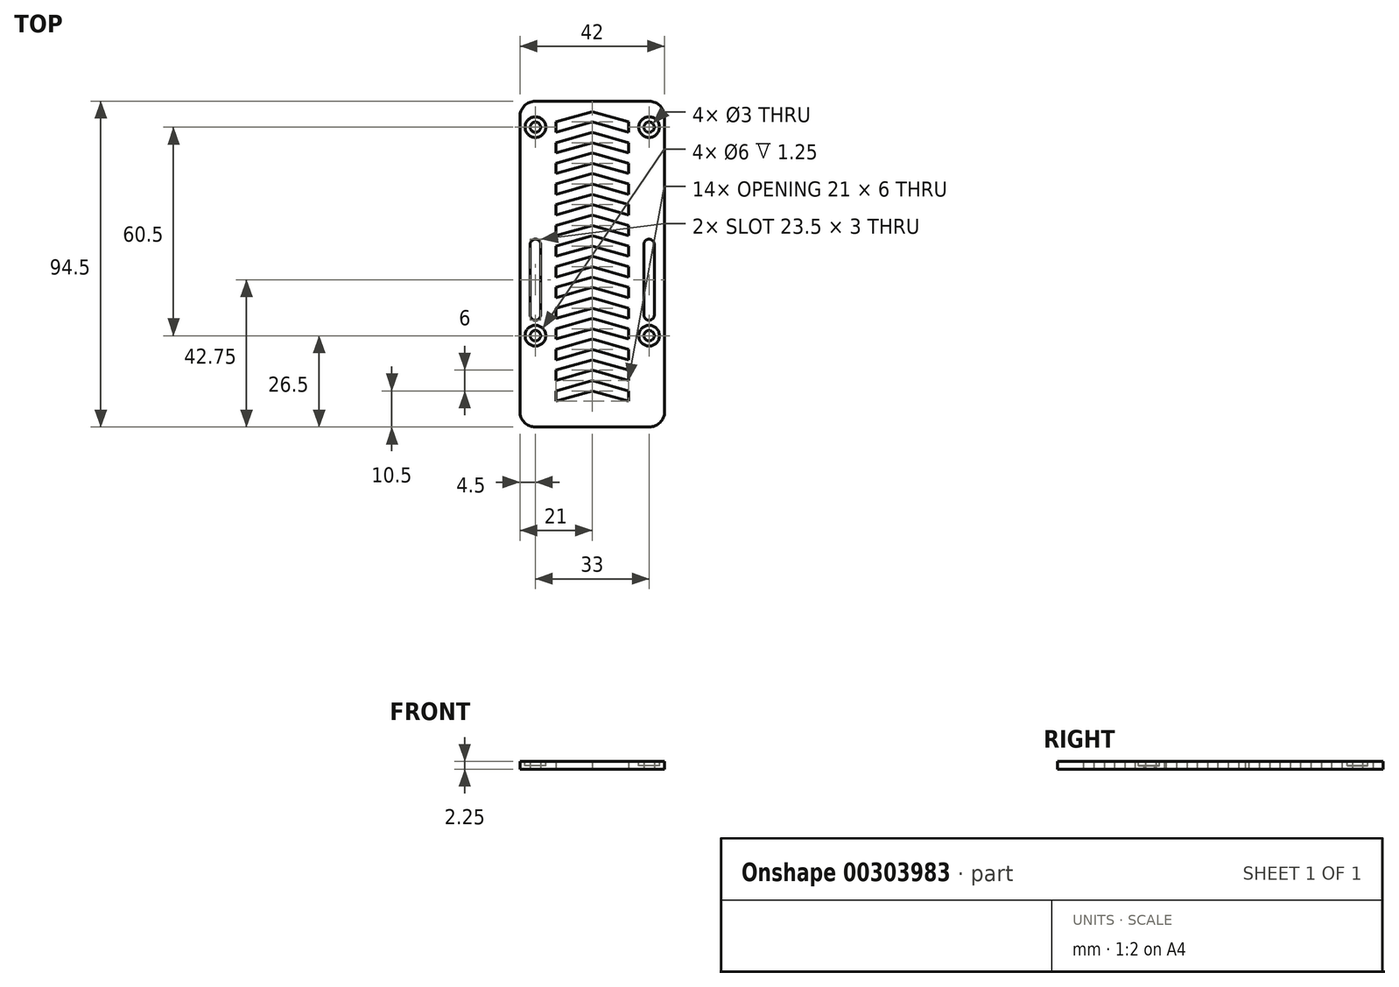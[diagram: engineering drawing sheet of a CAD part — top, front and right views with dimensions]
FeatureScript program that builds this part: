
annotation { "Feature Type Name" : "Feature", "Feature Type Description" : "" }
export const myFeature = defineFeature(function(context is Context, id is Id, definition is map)
    precondition{}
    {
        {
            var Q0;
            Q0=qCreatedBy(makeId("Top.planeOp"),FACE);
            var sketch = newSketch(context, id + "F0", { "sketchPlane" : qUnion([Q0])});
            skLineSegment(sketch, "E0.left", {"start": v(-21, 35.25) * mm, "end": v(-21, -44.25) * mm});
            skLineSegment(sketch, "E0.right", {"start": v(21, 35.25) * mm, "end": v(21, -44.25) * mm});
            skLineSegment(sketch, "E1", {"start": v(-16.5, -0.25) * mm, "end": v(-16.5, -0.25) * mm});
            skLineSegment(sketch, "E2", {"start": v(-16.5, -23.75) * mm, "end": v(-16.5, -23.75) * mm});
            skLineSegment(sketch, "E3", {"start": v(16.5, -23.75) * mm, "end": v(16.5, -23.75) * mm});
            skLineSegment(sketch, "E4", {"start": v(16.5, -0.25) * mm, "end": v(16.5, -0.25) * mm});
            skLineSegment(sketch, "E5.trimOffspring", {"start": v(18, -1.75) * mm, "end": v(18, -22.25) * mm});
            skLineSegment(sketch, "E6.trimOffspring", {"start": v(15, -1.75) * mm, "end": v(15, -22.25) * mm});
            skLineSegment(sketch, "E7.trimOffspring", {"start": v(-15, -1.75) * mm, "end": v(-15, -22.25) * mm});
            skLineSegment(sketch, "E8.trimOffspring", {"start": v(-18, -1.75) * mm, "end": v(-18, -22.25) * mm});
            skCircle(sketch, "E9", {"center": v(16.5, 32.25) * mm, "radius": 1.5 * mm});
            skCircle(sketch, "E10", {"center": v(-16.5, 32.25) * mm, "radius": 1.5 * mm});
            skPoint(sketch, "E11.visualSharp", {"position": v(18, -0.25) * mm});
            skArc(sketch, "E11.filletArc", {"start": v(18, -1.75) * mm, "mid": v(17.56, -0.69) * mm, "end": v(16.5, -0.25) * mm});
            skPoint(sketch, "E12.visualSharp", {"position": v(15, -0.25) * mm});
            skArc(sketch, "E12.filletArc", {"start": v(16.5, -0.25) * mm, "mid": v(15.44, -0.69) * mm, "end": v(15, -1.75) * mm});
            skPoint(sketch, "E13.visualSharp", {"position": v(-15, -0.25) * mm});
            skArc(sketch, "E13.filletArc", {"start": v(-15, -1.75) * mm, "mid": v(-15.44, -0.69) * mm, "end": v(-16.5, -0.25) * mm});
            skPoint(sketch, "E14.visualSharp", {"position": v(-18, -0.25) * mm});
            skArc(sketch, "E14.filletArc", {"start": v(-16.5, -0.25) * mm, "mid": v(-17.56, -0.69) * mm, "end": v(-18, -1.75) * mm});
            skCircle(sketch, "E15", {"center": v(16.5, -28.25) * mm, "radius": 1.5 * mm});
            skPoint(sketch, "E15.centerSnap0", {"position": v(16.5, -23.75) * mm});
            skCircle(sketch, "E16", {"center": v(-16.5, -28.25) * mm, "radius": 1.5 * mm});
            skPoint(sketch, "E16.centerSnap0", {"position": v(-16.5, -23.75) * mm});
            skPoint(sketch, "E17.visualSharp", {"position": v(18, -23.75) * mm});
            skArc(sketch, "E17.filletArc", {"start": v(16.5, -23.75) * mm, "mid": v(17.56, -23.31) * mm, "end": v(18, -22.25) * mm});
            skPoint(sketch, "E18.visualSharp", {"position": v(-15, -23.75) * mm});
            skArc(sketch, "E18.filletArc", {"start": v(-16.5, -23.75) * mm, "mid": v(-15.44, -23.31) * mm, "end": v(-15, -22.25) * mm});
            skPoint(sketch, "E19.visualSharp", {"position": v(-18, -23.75) * mm});
            skArc(sketch, "E19.filletArc", {"start": v(-18, -22.25) * mm, "mid": v(-17.56, -23.31) * mm, "end": v(-16.5, -23.75) * mm});
            skPoint(sketch, "E20.visualSharp", {"position": v(15, -23.75) * mm});
            skArc(sketch, "E20.filletArc", {"start": v(15, -22.25) * mm, "mid": v(15.44, -23.31) * mm, "end": v(16.5, -23.75) * mm});
            skPoint(sketch, "E21", {"position": v(-21, -54.75) * mm});
            skLineSegment(sketch, "E22", {"start": v(-21, -44.25) * mm, "end": v(-21, -50.25) * mm});
            skLineSegment(sketch, "E23", {"start": v(21, -44.25) * mm, "end": v(21, -50.25) * mm});
            skLineSegment(sketch, "E24", {"start": v(16.5, -54.75) * mm, "end": v(-16.5, -54.75) * mm});
            skArc(sketch, "E25.filletArc", {"start": v(-21, -50.25) * mm, "mid": v(-19.68, -53.43) * mm, "end": v(-16.5, -54.75) * mm});
            skPoint(sketch, "E26.visualSharp", {"position": v(21, -54.75) * mm});
            skArc(sketch, "E26.filletArc", {"start": v(16.5, -54.75) * mm, "mid": v(19.68, -53.43) * mm, "end": v(21, -50.25) * mm});
            skLineSegment(sketch, "E27", {"start": v(-16.5, 39.75) * mm, "end": v(16.5, 39.75) * mm});
            skPoint(sketch, "E28.visualSharp", {"position": v(-21, 39.75) * mm});
            skArc(sketch, "E28.filletArc", {"start": v(-16.5, 39.75) * mm, "mid": v(-19.68, 38.43) * mm, "end": v(-21, 35.25) * mm});
            skPoint(sketch, "E29.visualSharp", {"position": v(21, 39.75) * mm});
            skArc(sketch, "E29.filletArc", {"start": v(21, 35.25) * mm, "mid": v(19.68, 38.43) * mm, "end": v(16.5, 39.75) * mm});
            skCircle(sketch, "E30", {"center": v(-16.5, 32.25) * mm, "radius": 3 * mm, "construction": true});
            skCircle(sketch, "E31", {"center": v(16.5, 32.25) * mm, "radius": 3 * mm, "construction": true});
            skPoint(sketch, "E32", {"position": v(-10.5, 36.75) * mm});
            skPoint(sketch, "E33", {"position": v(-10.5, 33.75) * mm});
            skPoint(sketch, "E34", {"position": v(-10.5, 30.75) * mm});
            skPoint(sketch, "E35", {"position": v(-10.5, 27.75) * mm});
            skPoint(sketch, "E36", {"position": v(-10.5, 24.75) * mm});
            skLineSegment(sketch, "E37", {"start": v(0, 36.75) * mm, "end": v(-10.5, 33.75) * mm});
            skPoint(sketch, "E37.startSnap0", {"position": v(0, 39.75) * mm});
            skLineSegment(sketch, "E38", {"start": v(-10.5, 30.75) * mm, "end": v(-10.5, 33.75) * mm});
            skLineSegment(sketch, "E39", {"start": v(0, 33.75) * mm, "end": v(-10.5, 30.75) * mm});
            skLineSegment(sketch, "E40", {"start": v(0, 33.75) * mm, "end": v(10.5, 30.75) * mm});
            skLineSegment(sketch, "E41", {"start": v(10.5, 30.75) * mm, "end": v(10.5, 33.75) * mm});
            skLineSegment(sketch, "E42", {"start": v(10.5, 33.75) * mm, "end": v(0, 36.75) * mm});
            skLineSegment(sketch, "E43.1.0.0", {"start": v(0, 30.75) * mm, "end": v(-10.5, 27.75) * mm});
            skLineSegment(sketch, "E43.1.0.1", {"start": v(-10.5, 24.75) * mm, "end": v(-10.5, 27.75) * mm});
            skLineSegment(sketch, "E43.1.0.2", {"start": v(0, 27.75) * mm, "end": v(-10.5, 24.75) * mm});
            skLineSegment(sketch, "E43.1.0.3", {"start": v(0, 27.75) * mm, "end": v(10.5, 24.75) * mm});
            skLineSegment(sketch, "E43.1.0.4", {"start": v(10.5, 24.75) * mm, "end": v(10.5, 27.75) * mm});
            skLineSegment(sketch, "E43.1.0.5", {"start": v(10.5, 27.75) * mm, "end": v(0, 30.75) * mm});
            skLineSegment(sketch, "E43.2.0.0", {"start": v(0, 24.75) * mm, "end": v(-10.5, 21.75) * mm});
            skLineSegment(sketch, "E43.2.0.1", {"start": v(-10.5, 18.75) * mm, "end": v(-10.5, 21.75) * mm});
            skLineSegment(sketch, "E43.2.0.2", {"start": v(0, 21.75) * mm, "end": v(-10.5, 18.75) * mm});
            skLineSegment(sketch, "E43.2.0.3", {"start": v(0, 21.75) * mm, "end": v(10.5, 18.75) * mm});
            skLineSegment(sketch, "E43.2.0.4", {"start": v(10.5, 18.75) * mm, "end": v(10.5, 21.75) * mm});
            skLineSegment(sketch, "E43.2.0.5", {"start": v(10.5, 21.75) * mm, "end": v(0, 24.75) * mm});
            skLineSegment(sketch, "E43.3.0.0", {"start": v(0, 18.75) * mm, "end": v(-10.5, 15.75) * mm});
            skLineSegment(sketch, "E43.3.0.1", {"start": v(-10.5, 12.75) * mm, "end": v(-10.5, 15.75) * mm});
            skLineSegment(sketch, "E43.3.0.2", {"start": v(0, 15.75) * mm, "end": v(-10.5, 12.75) * mm});
            skLineSegment(sketch, "E43.3.0.3", {"start": v(0, 15.75) * mm, "end": v(10.5, 12.75) * mm});
            skLineSegment(sketch, "E43.3.0.4", {"start": v(10.5, 12.75) * mm, "end": v(10.5, 15.75) * mm});
            skLineSegment(sketch, "E43.3.0.5", {"start": v(10.5, 15.75) * mm, "end": v(0, 18.75) * mm});
            skLineSegment(sketch, "E43.4.0.0", {"start": v(0, 12.75) * mm, "end": v(-10.5, 9.75) * mm});
            skLineSegment(sketch, "E43.4.0.1", {"start": v(-10.5, 6.75) * mm, "end": v(-10.5, 9.75) * mm});
            skLineSegment(sketch, "E43.4.0.2", {"start": v(0, 9.75) * mm, "end": v(-10.5, 6.75) * mm});
            skLineSegment(sketch, "E43.4.0.3", {"start": v(0, 9.75) * mm, "end": v(10.5, 6.75) * mm});
            skLineSegment(sketch, "E43.4.0.4", {"start": v(10.5, 6.75) * mm, "end": v(10.5, 9.75) * mm});
            skLineSegment(sketch, "E43.4.0.5", {"start": v(10.5, 9.75) * mm, "end": v(0, 12.75) * mm});
            skLineSegment(sketch, "E43.5.0.0", {"start": v(0, 6.75) * mm, "end": v(-10.5, 3.75) * mm});
            skLineSegment(sketch, "E43.5.0.1", {"start": v(-10.5, 0.75) * mm, "end": v(-10.5, 3.75) * mm});
            skLineSegment(sketch, "E43.5.0.2", {"start": v(0, 3.75) * mm, "end": v(-10.5, 0.75) * mm});
            skLineSegment(sketch, "E43.5.0.3", {"start": v(0, 3.75) * mm, "end": v(10.5, 0.75) * mm});
            skLineSegment(sketch, "E43.5.0.4", {"start": v(10.5, 0.75) * mm, "end": v(10.5, 3.75) * mm});
            skLineSegment(sketch, "E43.5.0.5", {"start": v(10.5, 3.75) * mm, "end": v(0, 6.75) * mm});
            skLineSegment(sketch, "E43.6.0.0", {"start": v(0, 0.75) * mm, "end": v(-10.5, -2.25) * mm});
            skLineSegment(sketch, "E43.6.0.1", {"start": v(-10.5, -5.25) * mm, "end": v(-10.5, -2.25) * mm});
            skLineSegment(sketch, "E43.6.0.2", {"start": v(0, -2.25) * mm, "end": v(-10.5, -5.25) * mm});
            skLineSegment(sketch, "E43.6.0.3", {"start": v(0, -2.25) * mm, "end": v(10.5, -5.25) * mm});
            skLineSegment(sketch, "E43.6.0.4", {"start": v(10.5, -5.25) * mm, "end": v(10.5, -2.25) * mm});
            skLineSegment(sketch, "E43.6.0.5", {"start": v(10.5, -2.25) * mm, "end": v(0, 0.75) * mm});
            skLineSegment(sketch, "E43.7.0.0", {"start": v(0, -5.25) * mm, "end": v(-10.5, -8.25) * mm});
            skLineSegment(sketch, "E43.7.0.1", {"start": v(-10.5, -11.25) * mm, "end": v(-10.5, -8.25) * mm});
            skLineSegment(sketch, "E43.7.0.2", {"start": v(0, -8.25) * mm, "end": v(-10.5, -11.25) * mm});
            skLineSegment(sketch, "E43.7.0.3", {"start": v(0, -8.25) * mm, "end": v(10.5, -11.25) * mm});
            skLineSegment(sketch, "E43.7.0.4", {"start": v(10.5, -11.25) * mm, "end": v(10.5, -8.25) * mm});
            skLineSegment(sketch, "E43.7.0.5", {"start": v(10.5, -8.25) * mm, "end": v(0, -5.25) * mm});
            skLineSegment(sketch, "E43.8.0.0", {"start": v(0, -11.25) * mm, "end": v(-10.5, -14.25) * mm});
            skLineSegment(sketch, "E43.8.0.1", {"start": v(-10.5, -17.25) * mm, "end": v(-10.5, -14.25) * mm});
            skLineSegment(sketch, "E43.8.0.2", {"start": v(0, -14.25) * mm, "end": v(-10.5, -17.25) * mm});
            skLineSegment(sketch, "E43.8.0.3", {"start": v(0, -14.25) * mm, "end": v(10.5, -17.25) * mm});
            skLineSegment(sketch, "E43.8.0.4", {"start": v(10.5, -17.25) * mm, "end": v(10.5, -14.25) * mm});
            skLineSegment(sketch, "E43.8.0.5", {"start": v(10.5, -14.25) * mm, "end": v(0, -11.25) * mm});
            skLineSegment(sketch, "E43.9.0.0", {"start": v(0, -17.25) * mm, "end": v(-10.5, -20.25) * mm});
            skLineSegment(sketch, "E43.9.0.1", {"start": v(-10.5, -23.25) * mm, "end": v(-10.5, -20.25) * mm});
            skLineSegment(sketch, "E43.9.0.2", {"start": v(0, -20.25) * mm, "end": v(-10.5, -23.25) * mm});
            skLineSegment(sketch, "E43.9.0.3", {"start": v(0, -20.25) * mm, "end": v(10.5, -23.25) * mm});
            skLineSegment(sketch, "E43.9.0.4", {"start": v(10.5, -23.25) * mm, "end": v(10.5, -20.25) * mm});
            skLineSegment(sketch, "E43.9.0.5", {"start": v(10.5, -20.25) * mm, "end": v(0, -17.25) * mm});
            skLineSegment(sketch, "E43.10.0.0", {"start": v(0, -23.25) * mm, "end": v(-10.5, -26.25) * mm});
            skLineSegment(sketch, "E43.10.0.1", {"start": v(-10.5, -29.25) * mm, "end": v(-10.5, -26.25) * mm});
            skLineSegment(sketch, "E43.10.0.2", {"start": v(0, -26.25) * mm, "end": v(-10.5, -29.25) * mm});
            skLineSegment(sketch, "E43.10.0.3", {"start": v(0, -26.25) * mm, "end": v(10.5, -29.25) * mm});
            skLineSegment(sketch, "E43.10.0.4", {"start": v(10.5, -29.25) * mm, "end": v(10.5, -26.25) * mm});
            skLineSegment(sketch, "E43.10.0.5", {"start": v(10.5, -26.25) * mm, "end": v(0, -23.25) * mm});
            skLineSegment(sketch, "E43.11.0.0", {"start": v(0, -29.25) * mm, "end": v(-10.5, -32.25) * mm});
            skLineSegment(sketch, "E43.11.0.1", {"start": v(-10.5, -35.25) * mm, "end": v(-10.5, -32.25) * mm});
            skLineSegment(sketch, "E43.11.0.2", {"start": v(0, -32.25) * mm, "end": v(-10.5, -35.25) * mm});
            skLineSegment(sketch, "E43.11.0.3", {"start": v(0, -32.25) * mm, "end": v(10.5, -35.25) * mm});
            skLineSegment(sketch, "E43.11.0.4", {"start": v(10.5, -35.25) * mm, "end": v(10.5, -32.25) * mm});
            skLineSegment(sketch, "E43.11.0.5", {"start": v(10.5, -32.25) * mm, "end": v(0, -29.25) * mm});
            skLineSegment(sketch, "E43.12.0.0", {"start": v(0, -35.25) * mm, "end": v(-10.5, -38.25) * mm});
            skLineSegment(sketch, "E43.12.0.1", {"start": v(-10.5, -41.25) * mm, "end": v(-10.5, -38.25) * mm});
            skLineSegment(sketch, "E43.12.0.2", {"start": v(0, -38.25) * mm, "end": v(-10.5, -41.25) * mm});
            skLineSegment(sketch, "E43.12.0.3", {"start": v(0, -38.25) * mm, "end": v(10.5, -41.25) * mm});
            skLineSegment(sketch, "E43.12.0.4", {"start": v(10.5, -41.25) * mm, "end": v(10.5, -38.25) * mm});
            skLineSegment(sketch, "E43.12.0.5", {"start": v(10.5, -38.25) * mm, "end": v(0, -35.25) * mm});
            skLineSegment(sketch, "E43.13.0.0", {"start": v(0, -41.25) * mm, "end": v(-10.5, -44.25) * mm});
            skLineSegment(sketch, "E43.13.0.1", {"start": v(-10.5, -47.25) * mm, "end": v(-10.5, -44.25) * mm});
            skLineSegment(sketch, "E43.13.0.2", {"start": v(0, -44.25) * mm, "end": v(-10.5, -47.25) * mm});
            skLineSegment(sketch, "E43.13.0.3", {"start": v(0, -44.25) * mm, "end": v(10.5, -47.25) * mm});
            skLineSegment(sketch, "E43.13.0.4", {"start": v(10.5, -47.25) * mm, "end": v(10.5, -44.25) * mm});
            skLineSegment(sketch, "E43.13.0.5", {"start": v(10.5, -44.25) * mm, "end": v(0, -41.25) * mm});
            skLineSegment(sketch, "E43.direction1", {"start": v(-10.5, 33.75) * mm, "end": v(-10.5, 27.75) * mm, "construction": true});
            skSolve(sketch);
        }
        {
            var Q0;
            Q0 = qSketchRegion(id + "F0", true);
            extrude(context, id + "F1", {"entities" : qUnion([Q0]), "depth" : 2.25 * mm});
        }
        {
            var Q0;
            Q0=makeQuery(id+"F1.opExtrude","CAP_FACE",FACE,{"disambiguationData":[OSD([sQuery(id+"F0.wireOp",EDGE,"E0.left"),sQuery(id+"F0.wireOp",EDGE,"E0.right"),sQuery(id+"F0.wireOp",EDGE,"E5.trimOffspring"),sQuery(id+"F0.wireOp",EDGE,"E6.trimOffspring"),sQuery(id+"F0.wireOp",EDGE,"E7.trimOffspring"),sQuery(id+"F0.wireOp",EDGE,"E8.trimOffspring"),sQuery(id+"F0.wireOp",EDGE,"E9"),sQuery(id+"F0.wireOp",EDGE,"E10"),sQuery(id+"F0.wireOp",EDGE,"E11.filletArc"),sQuery(id+"F0.wireOp",EDGE,"E12.filletArc"),sQuery(id+"F0.wireOp",EDGE,"E13.filletArc"),sQuery(id+"F0.wireOp",EDGE,"E14.filletArc"),sQuery(id+"F0.wireOp",EDGE,"E15"),sQuery(id+"F0.wireOp",EDGE,"E16"),sQuery(id+"F0.wireOp",EDGE,"E17.filletArc"),sQuery(id+"F0.wireOp",EDGE,"E18.filletArc"),sQuery(id+"F0.wireOp",EDGE,"E19.filletArc"),sQuery(id+"F0.wireOp",EDGE,"E20.filletArc"),sQuery(id+"F0.wireOp",EDGE,"E22"),sQuery(id+"F0.wireOp",EDGE,"E23"),sQuery(id+"F0.wireOp",EDGE,"E24"),sQuery(id+"F0.wireOp",EDGE,"E25.filletArc"),sQuery(id+"F0.wireOp",EDGE,"E26.filletArc"),sQuery(id+"F0.wireOp",EDGE,"E27"),sQuery(id+"F0.wireOp",EDGE,"E28.filletArc"),sQuery(id+"F0.wireOp",EDGE,"E29.filletArc"),sQuery(id+"F0.wireOp",EDGE,"E37"),sQuery(id+"F0.wireOp",EDGE,"E38"),sQuery(id+"F0.wireOp",EDGE,"E39"),sQuery(id+"F0.wireOp",EDGE,"E40"),sQuery(id+"F0.wireOp",EDGE,"E41"),sQuery(id+"F0.wireOp",EDGE,"E42"),sQuery(id+"F0.wireOp",EDGE,"E43.1.0.0"),sQuery(id+"F0.wireOp",EDGE,"E43.1.0.1"),sQuery(id+"F0.wireOp",EDGE,"E43.1.0.2"),sQuery(id+"F0.wireOp",EDGE,"E43.1.0.3"),sQuery(id+"F0.wireOp",EDGE,"E43.1.0.4"),sQuery(id+"F0.wireOp",EDGE,"E43.1.0.5"),sQuery(id+"F0.wireOp",EDGE,"E43.2.0.0"),sQuery(id+"F0.wireOp",EDGE,"E43.2.0.1"),sQuery(id+"F0.wireOp",EDGE,"E43.2.0.2"),sQuery(id+"F0.wireOp",EDGE,"E43.2.0.3"),sQuery(id+"F0.wireOp",EDGE,"E43.2.0.4"),sQuery(id+"F0.wireOp",EDGE,"E43.2.0.5"),sQuery(id+"F0.wireOp",EDGE,"E43.3.0.0"),sQuery(id+"F0.wireOp",EDGE,"E43.3.0.1"),sQuery(id+"F0.wireOp",EDGE,"E43.3.0.2"),sQuery(id+"F0.wireOp",EDGE,"E43.3.0.3"),sQuery(id+"F0.wireOp",EDGE,"E43.3.0.4"),sQuery(id+"F0.wireOp",EDGE,"E43.3.0.5"),sQuery(id+"F0.wireOp",EDGE,"E43.4.0.0"),sQuery(id+"F0.wireOp",EDGE,"E43.4.0.1"),sQuery(id+"F0.wireOp",EDGE,"E43.4.0.2"),sQuery(id+"F0.wireOp",EDGE,"E43.4.0.3"),sQuery(id+"F0.wireOp",EDGE,"E43.4.0.4"),sQuery(id+"F0.wireOp",EDGE,"E43.4.0.5"),sQuery(id+"F0.wireOp",EDGE,"E43.5.0.0"),sQuery(id+"F0.wireOp",EDGE,"E43.5.0.1"),sQuery(id+"F0.wireOp",EDGE,"E43.5.0.2"),sQuery(id+"F0.wireOp",EDGE,"E43.5.0.3"),sQuery(id+"F0.wireOp",EDGE,"E43.5.0.4"),sQuery(id+"F0.wireOp",EDGE,"E43.5.0.5"),sQuery(id+"F0.wireOp",EDGE,"E43.6.0.0"),sQuery(id+"F0.wireOp",EDGE,"E43.6.0.1"),sQuery(id+"F0.wireOp",EDGE,"E43.6.0.2"),sQuery(id+"F0.wireOp",EDGE,"E43.6.0.3"),sQuery(id+"F0.wireOp",EDGE,"E43.6.0.4"),sQuery(id+"F0.wireOp",EDGE,"E43.6.0.5"),sQuery(id+"F0.wireOp",EDGE,"E43.7.0.0"),sQuery(id+"F0.wireOp",EDGE,"E43.7.0.1"),sQuery(id+"F0.wireOp",EDGE,"E43.7.0.2"),sQuery(id+"F0.wireOp",EDGE,"E43.7.0.3"),sQuery(id+"F0.wireOp",EDGE,"E43.7.0.4"),sQuery(id+"F0.wireOp",EDGE,"E43.7.0.5"),sQuery(id+"F0.wireOp",EDGE,"E43.8.0.0"),sQuery(id+"F0.wireOp",EDGE,"E43.8.0.1"),sQuery(id+"F0.wireOp",EDGE,"E43.8.0.2"),sQuery(id+"F0.wireOp",EDGE,"E43.8.0.3"),sQuery(id+"F0.wireOp",EDGE,"E43.8.0.4"),sQuery(id+"F0.wireOp",EDGE,"E43.8.0.5"),sQuery(id+"F0.wireOp",EDGE,"E43.9.0.0"),sQuery(id+"F0.wireOp",EDGE,"E43.9.0.1"),sQuery(id+"F0.wireOp",EDGE,"E43.9.0.2"),sQuery(id+"F0.wireOp",EDGE,"E43.9.0.3"),sQuery(id+"F0.wireOp",EDGE,"E43.9.0.4"),sQuery(id+"F0.wireOp",EDGE,"E43.9.0.5"),sQuery(id+"F0.wireOp",EDGE,"E43.10.0.0"),sQuery(id+"F0.wireOp",EDGE,"E43.10.0.1"),sQuery(id+"F0.wireOp",EDGE,"E43.10.0.2"),sQuery(id+"F0.wireOp",EDGE,"E43.10.0.3"),sQuery(id+"F0.wireOp",EDGE,"E43.10.0.4"),sQuery(id+"F0.wireOp",EDGE,"E43.10.0.5"),sQuery(id+"F0.wireOp",EDGE,"E43.11.0.0"),sQuery(id+"F0.wireOp",EDGE,"E43.11.0.1"),sQuery(id+"F0.wireOp",EDGE,"E43.11.0.2"),sQuery(id+"F0.wireOp",EDGE,"E43.11.0.3"),sQuery(id+"F0.wireOp",EDGE,"E43.11.0.4"),sQuery(id+"F0.wireOp",EDGE,"E43.11.0.5"),sQuery(id+"F0.wireOp",EDGE,"E43.12.0.0"),sQuery(id+"F0.wireOp",EDGE,"E43.12.0.1"),sQuery(id+"F0.wireOp",EDGE,"E43.12.0.2"),sQuery(id+"F0.wireOp",EDGE,"E43.12.0.3"),sQuery(id+"F0.wireOp",EDGE,"E43.12.0.4"),sQuery(id+"F0.wireOp",EDGE,"E43.12.0.5"),sQuery(id+"F0.wireOp",EDGE,"E43.13.0.0"),sQuery(id+"F0.wireOp",EDGE,"E43.13.0.1"),sQuery(id+"F0.wireOp",EDGE,"E43.13.0.2"),sQuery(id+"F0.wireOp",EDGE,"E43.13.0.3"),sQuery(id+"F0.wireOp",EDGE,"E43.13.0.4"),sQuery(id+"F0.wireOp",EDGE,"E43.13.0.5")])],"isStart":false});
            var sketch = newSketch(context, id + "F2", { "sketchPlane" : qUnion([Q0])});
            skCircle(sketch, "E44", {"center": v(-16.5, -28.25) * mm, "radius": 3 * mm});
            skCircle(sketch, "E45", {"center": v(16.5, -28.25) * mm, "radius": 3 * mm});
            skCircle(sketch, "E46", {"center": v(16.5, 32.25) * mm, "radius": 3 * mm});
            skCircle(sketch, "E47", {"center": v(-16.5, 32.25) * mm, "radius": 3 * mm});
            skSolve(sketch);
        }
        {
            var Q0;
            Q0 = qSketchRegion(id + "F2", true);
            extrude(context, id + "F3", {"entities" : qUnion([Q0]), "operationType" : NewBodyOperationType.REMOVE, "oppositeDirection" : true, "depth" : 1.25 * mm});
        }
    });
